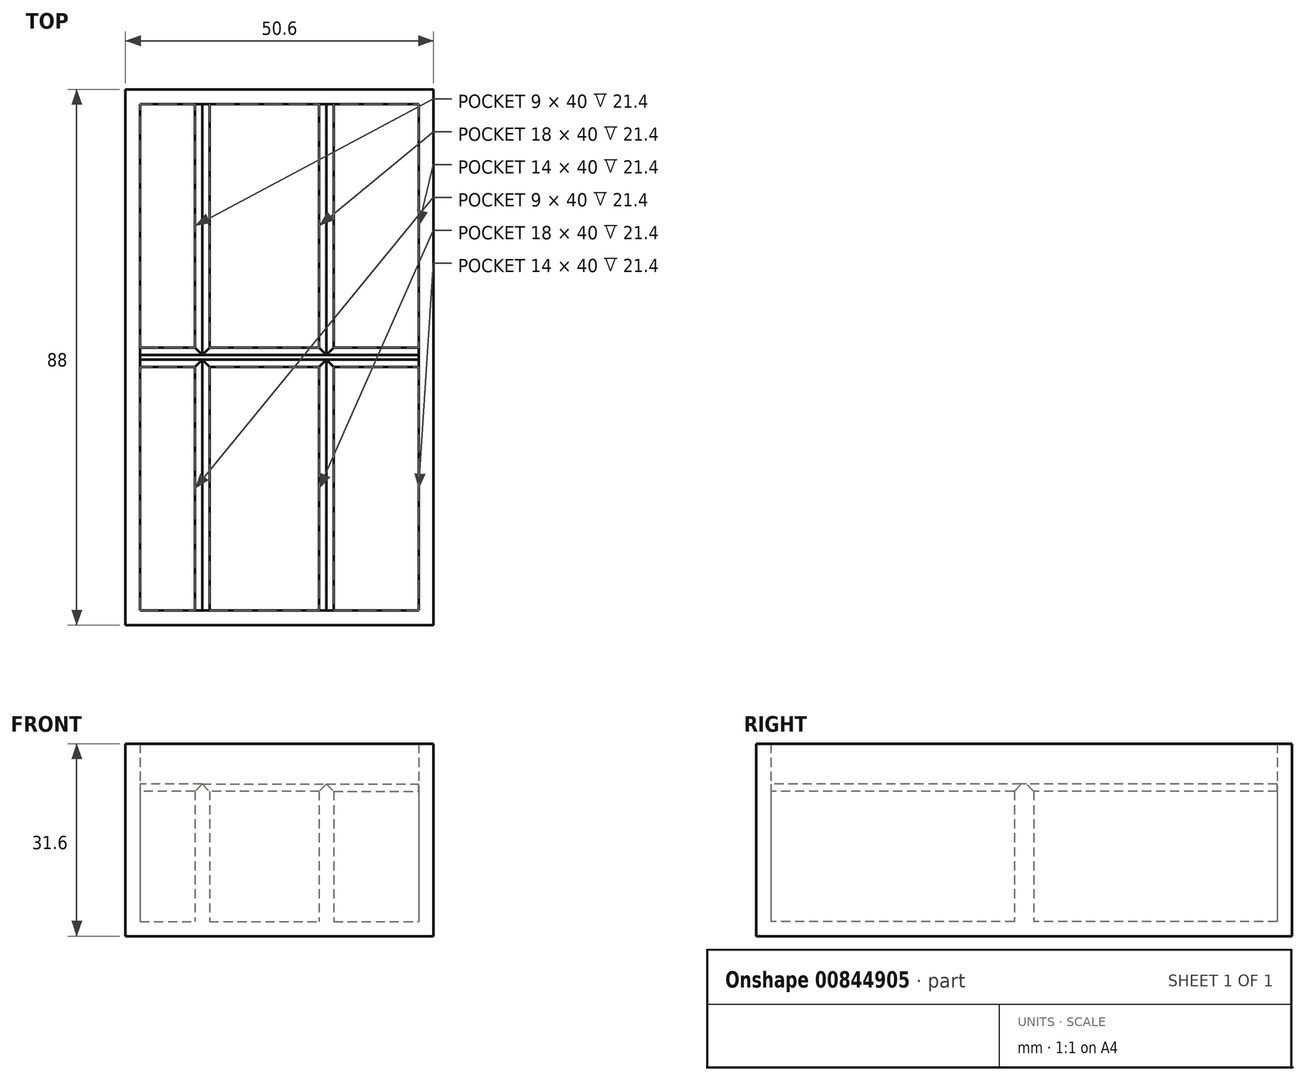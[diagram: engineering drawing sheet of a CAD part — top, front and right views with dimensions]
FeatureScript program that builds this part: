
annotation { "Feature Type Name" : "Feature", "Feature Type Description" : "" }
export const myFeature = defineFeature(function(context is Context, id is Id, definition is map)
    precondition{}
    {
        {
            var Q0;
            Q0=qCreatedBy(makeId("Top.planeOp"),FACE);
            var sketch = newSketch(context, id + "F0", { "sketchPlane" : qUnion([Q0])});
            skLineSegment(sketch, "E0.left", {"start": v(-60, 44) * mm, "end": v(-60, -44) * mm});
            skPoint(sketch, "E0.middle", {"position": v(0, 0) * mm});
            skLineSegment(sketch, "E1.0", {"start": v(-57.6, 41.6) * mm, "end": v(-57.6, -41.6) * mm});
            skLineSegment(sketch, "E2.0", {"start": v(-48.6, 41.6) * mm, "end": v(-48.6, -41.6) * mm});
            skLineSegment(sketch, "E3.0", {"start": v(-46.2, 41.6) * mm, "end": v(-46.2, -41.6) * mm});
            skLineSegment(sketch, "E4.0", {"start": v(-28.2, 41.6) * mm, "end": v(-28.2, -41.6) * mm});
            skLineSegment(sketch, "E5.0", {"start": v(-25.8, 41.6) * mm, "end": v(-25.8, -41.6) * mm});
            skLineSegment(sketch, "E6.0", {"start": v(-11.8, 41.6) * mm, "end": v(-11.8, -41.6) * mm});
            skLineSegment(sketch, "E7.0", {"start": v(-9.4, 41.6) * mm, "end": v(-9.4, -41.6) * mm});
            skLineSegment(sketch, "E8", {"start": v(-9.4, 41.6) * mm, "end": v(-9.4, 44) * mm});
            skLineSegment(sketch, "E9", {"start": v(-9.4, 44) * mm, "end": v(-9.4, -44) * mm});
            skLineSegment(sketch, "E10", {"start": v(-60, 44) * mm, "end": v(-9.4, 44) * mm});
            skLineSegment(sketch, "E11", {"start": v(-9.4, 41.6) * mm, "end": v(-57.6, 41.6) * mm});
            skLineSegment(sketch, "E12", {"start": v(-60, -44) * mm, "end": v(-9.4, -44) * mm});
            skLineSegment(sketch, "E13", {"start": v(-9.4, -41.6) * mm, "end": v(-57.6, -41.6) * mm});
            skLineSegment(sketch, "E14.0", {"start": v(-9.4, 1.6) * mm, "end": v(-57.6, 1.6) * mm});
            skLineSegment(sketch, "E15.0", {"start": v(-9.4, -1.6) * mm, "end": v(-57.6, -1.6) * mm});
            skSolve(sketch);
        }
        {
            var Q0;
            Q0=makeQuery(id+"F0.imprint","IMPRINT",FACE,{"disambiguationData":[TD([[makeQuery(id+"F0.imprint","IMPRINT",EDGE,{"derivedFrom":sQuery(id+"F0.wireOp",EDGE,"E0.left")}),1.0]])]});
            var Q1;
            {var subQ0=sQuery(id+"F0.wireOp",EDGE,"E6.0");Q1=makeQuery(id+"F0.imprint","IMPRINT",FACE,{"disambiguationData":[TD([[makeQuery(id+"F0.imprint","IMPRINT",EDGE,{"derivedFrom":subQ0}),1.0]])]});}
            extrude(context, id + "F1", {"entities" : qUnion([Q0, Q1]), "depth" : 31.6 * mm, "offsetDistance" : 25 * mm});
        }
        {
            var Q0;
            {var subQ0=sQuery(id+"F0.wireOp",EDGE,"E1.0");Q0=makeQuery(id+"F0.imprint","IMPRINT",FACE,{"disambiguationData":[TD([[makeQuery(id+"F0.imprint","IMPRINT",EDGE,{"derivedFrom":subQ0}),1.0]])]});}
            var Q1;
            {var subQ0=sQuery(id+"F0.wireOp",EDGE,"E3.0");Q1=makeQuery(id+"F0.imprint","IMPRINT",FACE,{"disambiguationData":[TD([[makeQuery(id+"F0.imprint","IMPRINT",EDGE,{"derivedFrom":subQ0}),1.0]])]});}
            var Q2;
            {var subQ0=sQuery(id+"F0.wireOp",EDGE,"E5.0");Q2=makeQuery(id+"F0.imprint","IMPRINT",FACE,{"disambiguationData":[TD([[makeQuery(id+"F0.imprint","IMPRINT",EDGE,{"derivedFrom":subQ0}),1.0]])]});}
            extrude(context, id + "F2", {"entities" : qUnion([Q0, Q1, Q2]), "operationType" : NewBodyOperationType.ADD, "depth" : 2.4 * mm, "offsetDistance" : 25 * mm});
        }
        {
            var Q0;
            Q0 = qSketchRegion(id + "F0", true);
            var Q1;
            {var subQ0=sQuery(id+"F0.wireOp",EDGE,"E14.0");var subQ1=sQuery(id+"F0.wireOp",EDGE,"E1.0");var subQ2=makeQuery(id+"F0.imprint","INTERSECT",VERTEX,{"derivedFrom":[subQ1,subQ0]});Q1=makeQuery(id+"F0.imprint","IMPRINT",FACE,{"disambiguationData":[TD([[makeQuery(id+"F0.imprint","IMPRINT",EDGE,{"disambiguationData":[TD([[subQ2,-1.0]])],"derivedFrom":subQ1}),1.0]])]});}
            var Q2;
            {var subQ0=sQuery(id+"F0.wireOp",EDGE,"E14.0");var subQ1=sQuery(id+"F0.wireOp",EDGE,"E2.0");var subQ2=makeQuery(id+"F0.imprint","INTERSECT",VERTEX,{"derivedFrom":[subQ1,subQ0]});Q2=makeQuery(id+"F0.imprint","IMPRINT",FACE,{"disambiguationData":[TD([[makeQuery(id+"F0.imprint","IMPRINT",EDGE,{"disambiguationData":[TD([[subQ2,-1.0]])],"derivedFrom":subQ1}),1.0]])]});}
            var Q3;
            {var subQ0=sQuery(id+"F0.wireOp",EDGE,"E11");var subQ1=sQuery(id+"F0.wireOp",EDGE,"E2.0");var subQ2=makeQuery(id+"F0.imprint","INTERSECT",VERTEX,{"derivedFrom":[subQ1,subQ0]});Q3=makeQuery(id+"F0.imprint","IMPRINT",FACE,{"disambiguationData":[TD([[makeQuery(id+"F0.imprint","IMPRINT",EDGE,{"disambiguationData":[TD([[subQ2,-1.0]])],"derivedFrom":subQ1}),1.0]])]});}
            var Q4;
            {var subQ0=sQuery(id+"F0.wireOp",EDGE,"E13");var subQ1=sQuery(id+"F0.wireOp",EDGE,"E2.0");var subQ2=makeQuery(id+"F0.imprint","INTERSECT",VERTEX,{"derivedFrom":[subQ1,subQ0]});Q4=makeQuery(id+"F0.imprint","IMPRINT",FACE,{"disambiguationData":[TD([[makeQuery(id+"F0.imprint","IMPRINT",EDGE,{"disambiguationData":[TD([[subQ2,1.0]])],"derivedFrom":subQ1}),1.0]])]});}
            var Q5;
            {var subQ0=sQuery(id+"F0.wireOp",EDGE,"E14.0");var subQ1=sQuery(id+"F0.wireOp",EDGE,"E3.0");var subQ2=makeQuery(id+"F0.imprint","INTERSECT",VERTEX,{"derivedFrom":[subQ1,subQ0]});Q5=makeQuery(id+"F0.imprint","IMPRINT",FACE,{"disambiguationData":[TD([[makeQuery(id+"F0.imprint","IMPRINT",EDGE,{"disambiguationData":[TD([[subQ2,-1.0]])],"derivedFrom":subQ1}),1.0]])]});}
            var Q6;
            {var subQ0=sQuery(id+"F0.wireOp",EDGE,"E11");var subQ1=sQuery(id+"F0.wireOp",EDGE,"E4.0");var subQ2=makeQuery(id+"F0.imprint","INTERSECT",VERTEX,{"derivedFrom":[subQ1,subQ0]});Q6=makeQuery(id+"F0.imprint","IMPRINT",FACE,{"disambiguationData":[TD([[makeQuery(id+"F0.imprint","IMPRINT",EDGE,{"disambiguationData":[TD([[subQ2,-1.0]])],"derivedFrom":subQ1}),1.0]])]});}
            var Q7;
            {var subQ0=sQuery(id+"F0.wireOp",EDGE,"E14.0");var subQ1=sQuery(id+"F0.wireOp",EDGE,"E4.0");var subQ2=makeQuery(id+"F0.imprint","INTERSECT",VERTEX,{"derivedFrom":[subQ1,subQ0]});Q7=makeQuery(id+"F0.imprint","IMPRINT",FACE,{"disambiguationData":[TD([[makeQuery(id+"F0.imprint","IMPRINT",EDGE,{"disambiguationData":[TD([[subQ2,-1.0]])],"derivedFrom":subQ1}),1.0]])]});}
            var Q8;
            {var subQ0=sQuery(id+"F0.wireOp",EDGE,"E14.0");var subQ1=sQuery(id+"F0.wireOp",EDGE,"E5.0");var subQ2=makeQuery(id+"F0.imprint","INTERSECT",VERTEX,{"derivedFrom":[subQ1,subQ0]});Q8=makeQuery(id+"F0.imprint","IMPRINT",FACE,{"disambiguationData":[TD([[makeQuery(id+"F0.imprint","IMPRINT",EDGE,{"disambiguationData":[TD([[subQ2,-1.0]])],"derivedFrom":subQ1}),1.0]])]});}
            var Q9;
            {var subQ0=sQuery(id+"F0.wireOp",EDGE,"E13");var subQ1=sQuery(id+"F0.wireOp",EDGE,"E4.0");var subQ2=makeQuery(id+"F0.imprint","INTERSECT",VERTEX,{"derivedFrom":[subQ1,subQ0]});Q9=makeQuery(id+"F0.imprint","IMPRINT",FACE,{"disambiguationData":[TD([[makeQuery(id+"F0.imprint","IMPRINT",EDGE,{"disambiguationData":[TD([[subQ2,1.0]])],"derivedFrom":subQ1}),1.0]])]});}
            extrude(context, id + "F3", {"entities" : qUnion([Q0, Q1, Q2, Q3, Q4, Q5, Q6, Q7, Q8, Q9]), "operationType" : NewBodyOperationType.ADD, "depth" : 25 * mm, "offsetDistance" : 25 * mm});
        }
        {
            var Q0;
            {var subQ0=sQuery(id+"F0.wireOp",EDGE,"E14.0");Q0=makeQuery(id+"F3.opExtrude","CAP_EDGE",EDGE,{"disambiguationData":[OSD([subQ0]),TDD([makeQuery(id+"F0.imprint","IMPRINT",EDGE,{"disambiguationData":[TD([[makeQuery(id+"F0.imprint","INTERSECT",VERTEX,{"derivedFrom":[sQuery(id+"F0.wireOp",EDGE,"E1.0"),subQ0]}),1.0]])],"derivedFrom":subQ0})])],"isStart":false});}
            var Q1;
            {var subQ0=sQuery(id+"F0.wireOp",EDGE,"E15.0");Q1=makeQuery(id+"F3.opExtrude","CAP_EDGE",EDGE,{"disambiguationData":[OSD([subQ0]),TDD([makeQuery(id+"F0.imprint","IMPRINT",EDGE,{"disambiguationData":[TD([[makeQuery(id+"F0.imprint","INTERSECT",VERTEX,{"derivedFrom":[sQuery(id+"F0.wireOp",EDGE,"E1.0"),subQ0]}),1.0]])],"derivedFrom":subQ0})])],"isStart":false});}
            var Q2;
            {var subQ0=sQuery(id+"F0.wireOp",EDGE,"E3.0");Q2=makeQuery(id+"F3.opExtrude","CAP_EDGE",EDGE,{"disambiguationData":[OSD([subQ0]),TDD([makeQuery(id+"F0.imprint","IMPRINT",EDGE,{"disambiguationData":[TD([[makeQuery(id+"F0.imprint","INTERSECT",VERTEX,{"derivedFrom":[subQ0,sQuery(id+"F0.wireOp",EDGE,"E13")]}),1.0]])],"derivedFrom":subQ0})])],"isStart":false});}
            var Q3;
            {var subQ0=sQuery(id+"F0.wireOp",EDGE,"E2.0");Q3=makeQuery(id+"F3.opExtrude","CAP_EDGE",EDGE,{"disambiguationData":[OSD([subQ0]),TDD([makeQuery(id+"F0.imprint","IMPRINT",EDGE,{"disambiguationData":[TD([[makeQuery(id+"F0.imprint","INTERSECT",VERTEX,{"derivedFrom":[subQ0,sQuery(id+"F0.wireOp",EDGE,"E13")]}),1.0]])],"derivedFrom":subQ0})])],"isStart":false});}
            var Q4;
            {var subQ0=sQuery(id+"F0.wireOp",EDGE,"E2.0");Q4=makeQuery(id+"F3.opExtrude","CAP_EDGE",EDGE,{"disambiguationData":[OSD([subQ0]),TDD([makeQuery(id+"F0.imprint","IMPRINT",EDGE,{"disambiguationData":[TD([[makeQuery(id+"F0.imprint","INTERSECT",VERTEX,{"derivedFrom":[subQ0,sQuery(id+"F0.wireOp",EDGE,"E11")]}),-1.0]])],"derivedFrom":subQ0})])],"isStart":false});}
            var Q5;
            {var subQ0=sQuery(id+"F0.wireOp",EDGE,"E3.0");Q5=makeQuery(id+"F3.opExtrude","CAP_EDGE",EDGE,{"disambiguationData":[OSD([subQ0]),TDD([makeQuery(id+"F0.imprint","IMPRINT",EDGE,{"disambiguationData":[TD([[makeQuery(id+"F0.imprint","INTERSECT",VERTEX,{"derivedFrom":[subQ0,sQuery(id+"F0.wireOp",EDGE,"E11")]}),-1.0]])],"derivedFrom":subQ0})])],"isStart":false});}
            var Q6;
            {var subQ0=sQuery(id+"F0.wireOp",EDGE,"E14.0");Q6=makeQuery(id+"F3.opExtrude","CAP_EDGE",EDGE,{"disambiguationData":[OSD([subQ0]),TDD([makeQuery(id+"F0.imprint","IMPRINT",EDGE,{"disambiguationData":[TD([[makeQuery(id+"F0.imprint","INTERSECT",VERTEX,{"derivedFrom":[sQuery(id+"F0.wireOp",EDGE,"E3.0"),subQ0]}),1.0]])],"derivedFrom":subQ0})])],"isStart":false});}
            var Q7;
            {var subQ0=sQuery(id+"F0.wireOp",EDGE,"E15.0");Q7=makeQuery(id+"F3.opExtrude","CAP_EDGE",EDGE,{"disambiguationData":[OSD([subQ0]),TDD([makeQuery(id+"F0.imprint","IMPRINT",EDGE,{"disambiguationData":[TD([[makeQuery(id+"F0.imprint","INTERSECT",VERTEX,{"derivedFrom":[sQuery(id+"F0.wireOp",EDGE,"E3.0"),subQ0]}),1.0]])],"derivedFrom":subQ0})])],"isStart":false});}
            var Q8;
            {var subQ0=sQuery(id+"F0.wireOp",EDGE,"E4.0");Q8=makeQuery(id+"F3.opExtrude","CAP_EDGE",EDGE,{"disambiguationData":[OSD([subQ0]),TDD([makeQuery(id+"F0.imprint","IMPRINT",EDGE,{"disambiguationData":[TD([[makeQuery(id+"F0.imprint","INTERSECT",VERTEX,{"derivedFrom":[subQ0,sQuery(id+"F0.wireOp",EDGE,"E13")]}),1.0]])],"derivedFrom":subQ0})])],"isStart":false});}
            var Q9;
            {var subQ0=sQuery(id+"F0.wireOp",EDGE,"E5.0");Q9=makeQuery(id+"F3.opExtrude","CAP_EDGE",EDGE,{"disambiguationData":[OSD([subQ0]),TDD([makeQuery(id+"F0.imprint","IMPRINT",EDGE,{"disambiguationData":[TD([[makeQuery(id+"F0.imprint","INTERSECT",VERTEX,{"derivedFrom":[subQ0,sQuery(id+"F0.wireOp",EDGE,"E13")]}),1.0]])],"derivedFrom":subQ0})])],"isStart":false});}
            var Q10;
            {var subQ0=sQuery(id+"F0.wireOp",EDGE,"E15.0");Q10=makeQuery(id+"F3.opExtrude","CAP_EDGE",EDGE,{"disambiguationData":[OSD([subQ0]),TDD([makeQuery(id+"F0.imprint","IMPRINT",EDGE,{"disambiguationData":[TD([[makeQuery(id+"F0.imprint","INTERSECT",VERTEX,{"derivedFrom":[sQuery(id+"F0.wireOp",EDGE,"E5.0"),subQ0]}),1.0]])],"derivedFrom":subQ0})])],"isStart":false});}
            var Q11;
            {var subQ0=sQuery(id+"F0.wireOp",EDGE,"E14.0");Q11=makeQuery(id+"F3.opExtrude","CAP_EDGE",EDGE,{"disambiguationData":[OSD([subQ0]),TDD([makeQuery(id+"F0.imprint","IMPRINT",EDGE,{"disambiguationData":[TD([[makeQuery(id+"F0.imprint","INTERSECT",VERTEX,{"derivedFrom":[sQuery(id+"F0.wireOp",EDGE,"E5.0"),subQ0]}),1.0]])],"derivedFrom":subQ0})])],"isStart":false});}
            var Q12;
            {var subQ0=sQuery(id+"F0.wireOp",EDGE,"E5.0");Q12=makeQuery(id+"F3.opExtrude","CAP_EDGE",EDGE,{"disambiguationData":[OSD([subQ0]),TDD([makeQuery(id+"F0.imprint","IMPRINT",EDGE,{"disambiguationData":[TD([[makeQuery(id+"F0.imprint","INTERSECT",VERTEX,{"derivedFrom":[subQ0,sQuery(id+"F0.wireOp",EDGE,"E11")]}),-1.0]])],"derivedFrom":subQ0})])],"isStart":false});}
            var Q13;
            {var subQ0=sQuery(id+"F0.wireOp",EDGE,"E4.0");Q13=makeQuery(id+"F3.opExtrude","CAP_EDGE",EDGE,{"disambiguationData":[OSD([subQ0]),TDD([makeQuery(id+"F0.imprint","IMPRINT",EDGE,{"disambiguationData":[TD([[makeQuery(id+"F0.imprint","INTERSECT",VERTEX,{"derivedFrom":[subQ0,sQuery(id+"F0.wireOp",EDGE,"E11")]}),-1.0]])],"derivedFrom":subQ0})])],"isStart":false});}
            chamfer(context, id + "F4", {"entities" : qUnion([Q0, Q1, Q2, Q3, Q4, Q5, Q6, Q7, Q8, Q9, Q10, Q11, Q12, Q13]), "width" : 1.2 * mm, "tangentPropagation" : true});
        }
    });
